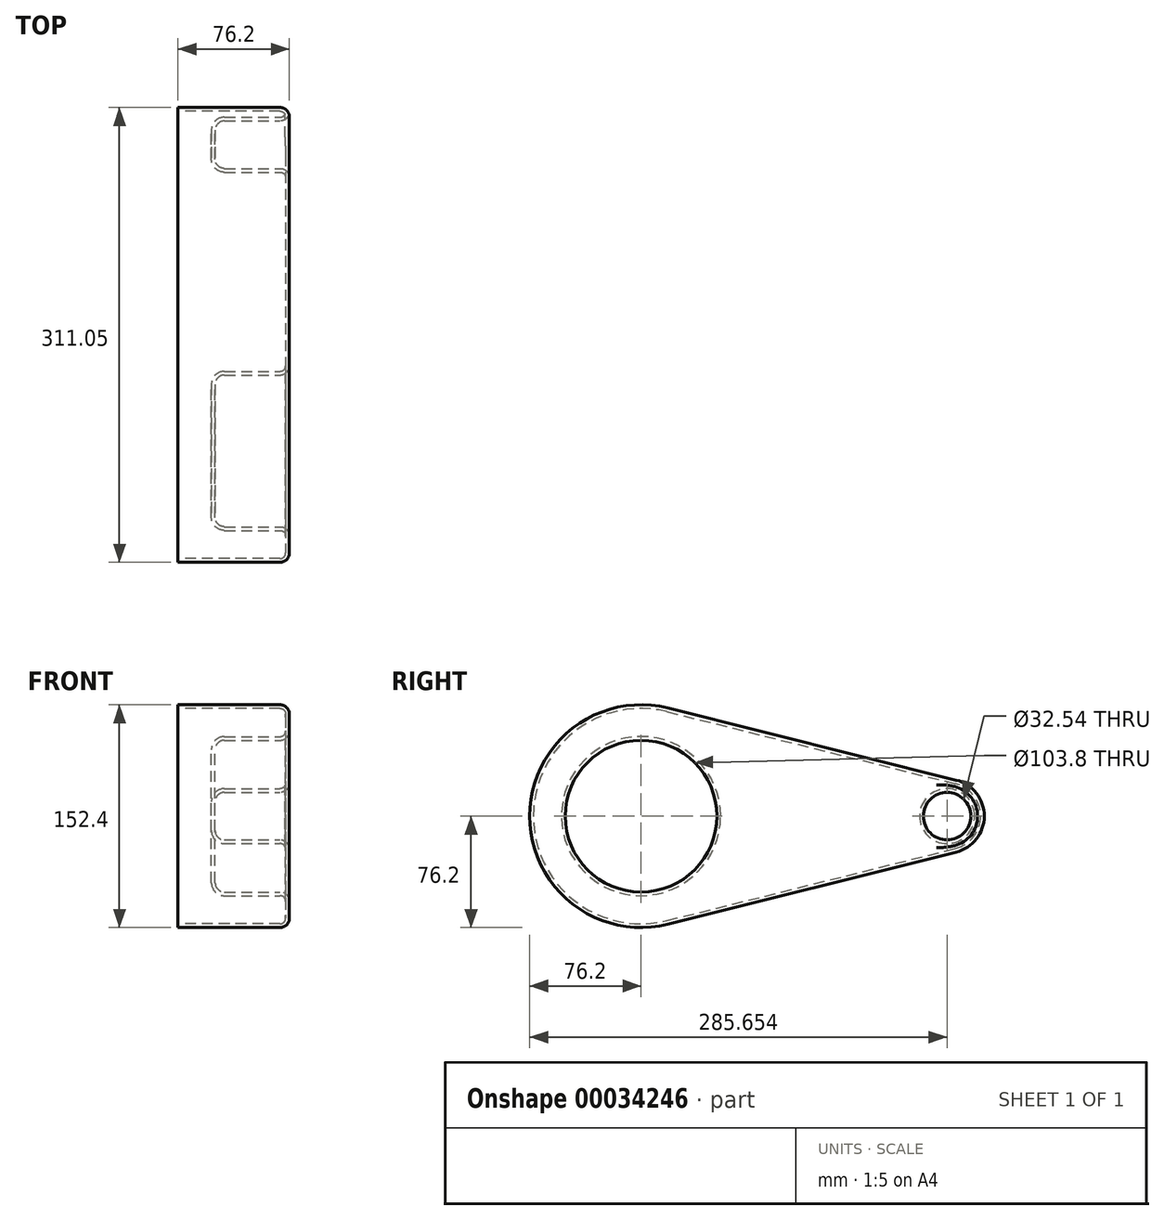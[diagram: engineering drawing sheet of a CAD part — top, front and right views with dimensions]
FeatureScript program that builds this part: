
annotation { "Feature Type Name" : "Feature", "Feature Type Description" : "" }
export const myFeature = defineFeature(function(context is Context, id is Id, definition is map)
    precondition{}
    {
        {
            var Q0;
            Q0=qCreatedBy(makeId("Right.planeOp"),FACE);
            var sketch = newSketch(context, id + "F0", { "sketchPlane" : qUnion([Q0])});
            skCircle(sketch, "E0", {"center": v(0, 0) * mm, "radius": 76.2 * mm});
            skCircle(sketch, "E1", {"center": v(209.45, 0) * mm, "radius": 25.4 * mm});
            skLineSegment(sketch, "E2", {"start": v(18.48, 73.92) * mm, "end": v(215.61, 24.64) * mm});
            skLineSegment(sketch, "E3", {"start": v(18.48, -73.92) * mm, "end": v(215.61, -24.64) * mm});
            skSolve(sketch);
        }
        {
            var Q0;
            Q0 = qSketchRegion(id + "F0", true);
            extrude(context, id + "F1", {"entities" : qUnion([Q0]), "depth" : 76.2 * mm});
        }
        {
            var Q0;
            Q0=makeQuery(id+"F1.opExtrude","CAP_FACE",FACE,{"disambiguationData":[OSD([sQuery(id+"F0.wireOp",EDGE,"E0"),sQuery(id+"F0.wireOp",EDGE,"E1"),sQuery(id+"F0.wireOp",EDGE,"E2"),sQuery(id+"F0.wireOp",EDGE,"E3")])],"isStart":false});
            var sketch = newSketch(context, id + "F2", { "sketchPlane" : qUnion([Q0])});
            skCircle(sketch, "E4", {"center": v(0, 0) * mm, "radius": 51.9 * mm});
            skCircle(sketch, "E5", {"center": v(209.45, 0) * mm, "radius": 16.27 * mm});
            skSolve(sketch);
        }
        {
            var Q0;
            Q0=makeQuery(id+"F2.imprint","IMPRINT",FACE,{"disambiguationData":[TD([[makeQuery(id+"F2.imprint","IMPRINT",EDGE,{"derivedFrom":sQuery(id+"F2.wireOp",EDGE,"E4")}),1.0]])]});
            var Q1;
            Q1=makeQuery(id+"F2.imprint","IMPRINT",FACE,{"disambiguationData":[TD([[makeQuery(id+"F2.imprint","IMPRINT",EDGE,{"derivedFrom":sQuery(id+"F2.wireOp",EDGE,"E5")}),1.0]])]});
            extrude(context, id + "F3", {"entities" : qUnion([Q0, Q1]), "operationType" : NewBodyOperationType.REMOVE, "oppositeDirection" : true, "depth" : 50.8 * mm});
        }
        {
            var Q0;
            Q0=makeQuery(id+"F1.opExtrude","CAP_FACE",FACE,{"disambiguationData":[OSD([sQuery(id+"F0.wireOp",EDGE,"E0"),sQuery(id+"F0.wireOp",EDGE,"E1"),sQuery(id+"F0.wireOp",EDGE,"E2"),sQuery(id+"F0.wireOp",EDGE,"E3")])],"isStart":false});
            var Q1;
            Q1=makeQuery(id+"F3.boolean.opBoolean","COPY",EDGE,{"derivedFrom":makeQuery(id+"F3.opExtrude","CAP_EDGE",EDGE,{"disambiguationData":[OSD([sQuery(id+"F2.wireOp",EDGE,"E4")])],"isStart":false})});
            var Q2;
            Q2=makeQuery(id+"F3.boolean.opBoolean","COPY",EDGE,{"derivedFrom":makeQuery(id+"F3.opExtrude","CAP_EDGE",EDGE,{"disambiguationData":[OSD([sQuery(id+"F2.wireOp",EDGE,"E5")])],"isStart":false})});
            fillet(context, id + "F4", {"entities" : qUnion([Q0, Q1, Q2]), "radius" : 6.35 * mm, "tangentPropagation" : true, "allowEdgeOverflow" : false});
        }
        {
            var Q0;
            Q0=makeQuery(id+"F1.opExtrude","CAP_FACE",FACE,{"disambiguationData":[OSD([sQuery(id+"F0.wireOp",EDGE,"E0"),sQuery(id+"F0.wireOp",EDGE,"E1"),sQuery(id+"F0.wireOp",EDGE,"E2"),sQuery(id+"F0.wireOp",EDGE,"E3")])],"isStart":true});
            shell(context, id + "F5", {"entities" : qUnion([Q0]), "thickness" : 2.54 * mm});
        }
    });
